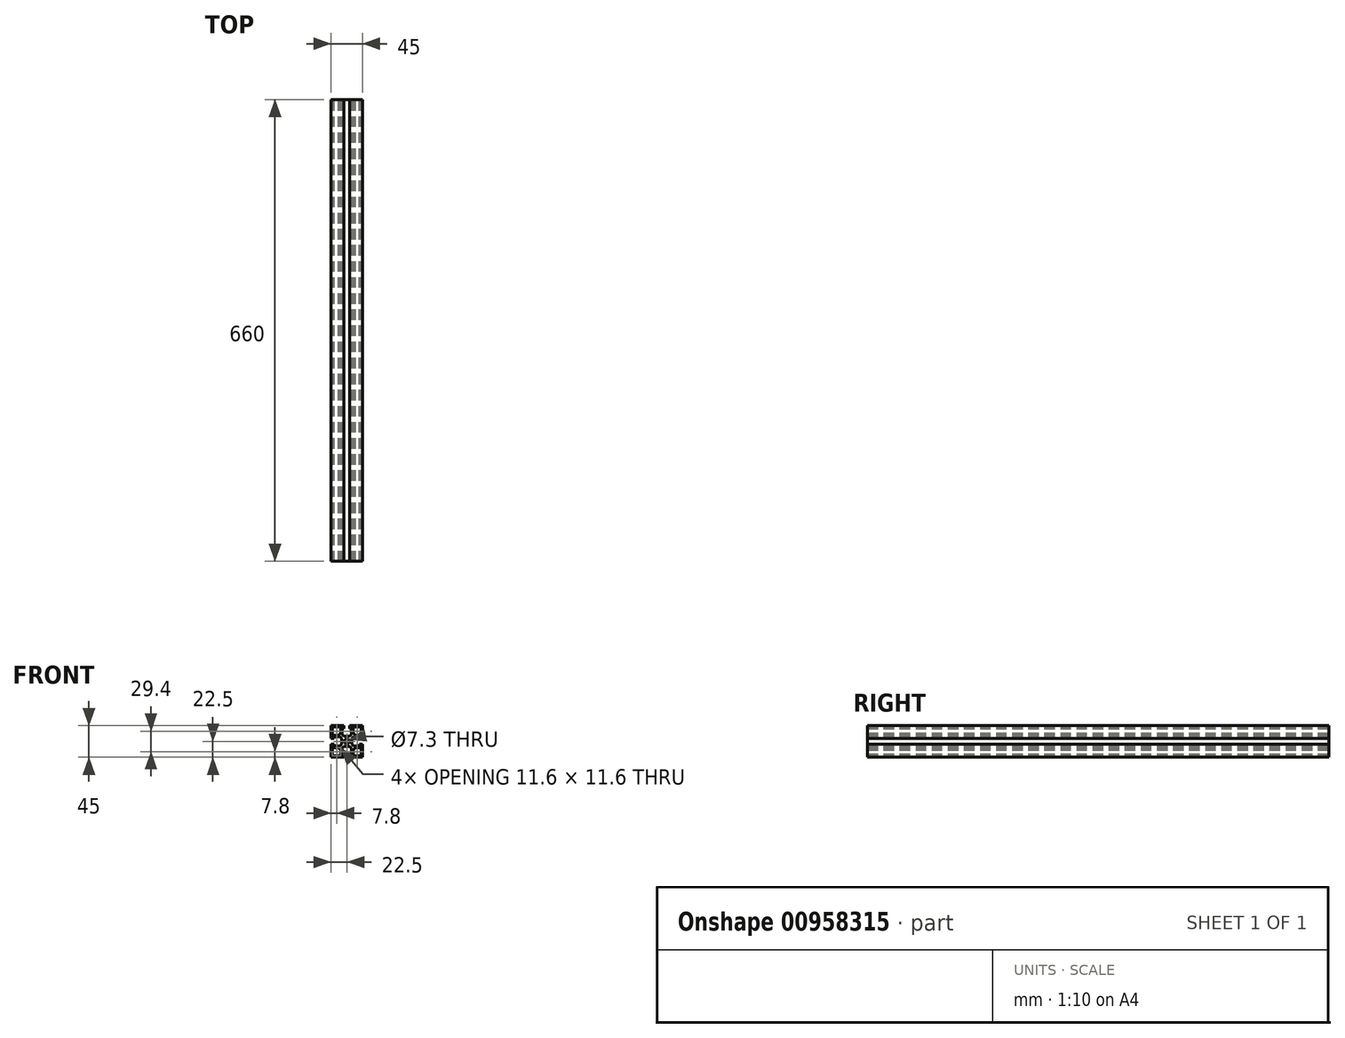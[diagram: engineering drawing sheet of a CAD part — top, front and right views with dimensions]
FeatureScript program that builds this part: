
annotation { "Feature Type Name" : "Feature", "Feature Type Description" : "" }
export const myFeature = defineFeature(function(context is Context, id is Id, definition is map)
    precondition{}
    {
        {
            var Q0;
            Q0=qCreatedBy(makeId("Front.planeOp"),FACE);
            var sketch = newSketch(context, id + "F0", { "sketchPlane" : qUnion([Q0])});
            skLineSegment(sketch, "E0", {"start": v(-22.5, 22.5) * mm, "end": v(-4.15, 22.5) * mm});
            skLineSegment(sketch, "E1", {"start": v(-4.15, 22.5) * mm, "end": v(-4.15, 18) * mm});
            skLineSegment(sketch, "E2", {"start": v(-4.15, 18) * mm, "end": v(-5.75, 18) * mm});
            skArc(sketch, "E3", {"start": v(-5.75, 18) * mm, "mid": v(-6.25, 18.5) * mm, "end": v(-6.75, 18) * mm});
            skLineSegment(sketch, "E4", {"start": v(-6.75, 18) * mm, "end": v(-6.75, 9.8) * mm});
            skLineSegment(sketch, "E5", {"start": v(-6.75, 9.8) * mm, "end": v(-4.15, 7.2) * mm});
            skLineSegment(sketch, "E6", {"start": v(-4.15, 7.2) * mm, "end": v(4.15, 7.2) * mm});
            skLineSegment(sketch, "E7", {"start": v(4.15, 7.2) * mm, "end": v(6.75, 9.8) * mm});
            skLineSegment(sketch, "E8", {"start": v(6.75, 9.8) * mm, "end": v(6.75, 18) * mm});
            skArc(sketch, "E9", {"start": v(6.75, 18) * mm, "mid": v(6.25, 18.5) * mm, "end": v(5.75, 18) * mm});
            skLineSegment(sketch, "E10", {"start": v(5.75, 18) * mm, "end": v(4.15, 18) * mm});
            skLineSegment(sketch, "E11", {"start": v(4.15, 18) * mm, "end": v(4.15, 22.5) * mm});
            skLineSegment(sketch, "E12", {"start": v(4.15, 22.5) * mm, "end": v(22.5, 22.5) * mm});
            skLineSegment(sketch, "E13", {"start": v(22.5, 22.5) * mm, "end": v(22.5, 4.15) * mm});
            skLineSegment(sketch, "E14", {"start": v(22.5, 4.15) * mm, "end": v(18, 4.15) * mm});
            skLineSegment(sketch, "E15", {"start": v(18, 4.15) * mm, "end": v(18, 5.75) * mm});
            skArc(sketch, "E16", {"start": v(18, 5.75) * mm, "mid": v(18.5, 6.25) * mm, "end": v(18, 6.75) * mm});
            skLineSegment(sketch, "E17", {"start": v(18, 6.75) * mm, "end": v(9.8, 6.75) * mm});
            skLineSegment(sketch, "E18", {"start": v(9.8, 6.75) * mm, "end": v(7.2, 4.15) * mm});
            skLineSegment(sketch, "E19", {"start": v(7.2, 4.15) * mm, "end": v(7.2, -4.15) * mm});
            skLineSegment(sketch, "E20", {"start": v(7.2, -4.15) * mm, "end": v(9.8, -6.75) * mm});
            skLineSegment(sketch, "E21", {"start": v(9.8, -6.75) * mm, "end": v(18, -6.75) * mm});
            skArc(sketch, "E22", {"start": v(18, -6.75) * mm, "mid": v(18.5, -6.25) * mm, "end": v(18, -5.75) * mm});
            skLineSegment(sketch, "E23", {"start": v(18, -5.75) * mm, "end": v(18, -4.15) * mm});
            skLineSegment(sketch, "E24", {"start": v(18, -4.15) * mm, "end": v(22.5, -4.15) * mm});
            skLineSegment(sketch, "E25", {"start": v(22.5, -4.15) * mm, "end": v(22.5, -22.5) * mm});
            skLineSegment(sketch, "E26", {"start": v(22.5, -22.5) * mm, "end": v(4.15, -22.5) * mm});
            skLineSegment(sketch, "E27", {"start": v(4.15, -22.5) * mm, "end": v(4.15, -18) * mm});
            skLineSegment(sketch, "E28", {"start": v(4.15, -18) * mm, "end": v(5.75, -18) * mm});
            skArc(sketch, "E29", {"start": v(5.75, -18) * mm, "mid": v(6.25, -18.5) * mm, "end": v(6.75, -18) * mm});
            skLineSegment(sketch, "E30", {"start": v(6.75, -18) * mm, "end": v(6.75, -9.8) * mm});
            skLineSegment(sketch, "E31", {"start": v(6.75, -9.8) * mm, "end": v(4.15, -7.2) * mm});
            skLineSegment(sketch, "E32", {"start": v(4.15, -7.2) * mm, "end": v(-4.15, -7.2) * mm});
            skLineSegment(sketch, "E33", {"start": v(-4.15, -7.2) * mm, "end": v(-6.75, -9.8) * mm});
            skLineSegment(sketch, "E34", {"start": v(-6.75, -9.8) * mm, "end": v(-6.75, -18) * mm});
            skArc(sketch, "E35", {"start": v(-6.75, -18) * mm, "mid": v(-6.25, -18.5) * mm, "end": v(-5.75, -18) * mm});
            skLineSegment(sketch, "E36", {"start": v(-5.75, -18) * mm, "end": v(-4.15, -18) * mm});
            skLineSegment(sketch, "E37", {"start": v(-4.15, -18) * mm, "end": v(-4.15, -22.5) * mm});
            skLineSegment(sketch, "E38", {"start": v(-4.15, -22.5) * mm, "end": v(-22.5, -22.5) * mm});
            skLineSegment(sketch, "E39", {"start": v(-22.5, -22.5) * mm, "end": v(-22.5, -4.15) * mm});
            skLineSegment(sketch, "E40", {"start": v(-22.5, -4.15) * mm, "end": v(-18, -4.15) * mm});
            skLineSegment(sketch, "E41", {"start": v(-18, -4.15) * mm, "end": v(-18, -5.75) * mm});
            skArc(sketch, "E42", {"start": v(-18, -5.75) * mm, "mid": v(-18.5, -6.25) * mm, "end": v(-18, -6.75) * mm});
            skLineSegment(sketch, "E43", {"start": v(-18, -6.75) * mm, "end": v(-9.8, -6.75) * mm});
            skLineSegment(sketch, "E44", {"start": v(-9.8, -6.75) * mm, "end": v(-7.2, -4.15) * mm});
            skLineSegment(sketch, "E45", {"start": v(-7.2, -4.15) * mm, "end": v(-7.2, 4.15) * mm});
            skLineSegment(sketch, "E46", {"start": v(-7.2, 4.15) * mm, "end": v(-9.8, 6.75) * mm});
            skLineSegment(sketch, "E47", {"start": v(-9.8, 6.75) * mm, "end": v(-18, 6.75) * mm});
            skArc(sketch, "E48", {"start": v(-18, 6.75) * mm, "mid": v(-18.5, 6.25) * mm, "end": v(-18, 5.75) * mm});
            skLineSegment(sketch, "E49", {"start": v(-18, 5.75) * mm, "end": v(-18, 4.15) * mm});
            skLineSegment(sketch, "E50", {"start": v(-18, 4.15) * mm, "end": v(-22.5, 4.15) * mm});
            skLineSegment(sketch, "E51", {"start": v(-22.5, 4.15) * mm, "end": v(-22.5, 22.5) * mm});
            skLineSegment(sketch, "E52", {"start": v(-19.5, 20.5) * mm, "end": v(-9.9, 20.5) * mm});
            skArc(sketch, "E53", {"start": v(-8.9, 19.5) * mm, "mid": v(-9.2, 20.2) * mm, "end": v(-9.9, 20.5) * mm});
            skLineSegment(sketch, "E54", {"start": v(-8.9, 19.5) * mm, "end": v(-8.9, 12.1) * mm});
            skLineSegment(sketch, "E55", {"start": v(-8.9, 12.1) * mm, "end": v(-12.1, 8.9) * mm});
            skLineSegment(sketch, "E56", {"start": v(-12.1, 8.9) * mm, "end": v(-19.5, 8.9) * mm});
            skArc(sketch, "E57", {"start": v(-20.5, 9.9) * mm, "mid": v(-20.2, 9.2) * mm, "end": v(-19.5, 8.9) * mm});
            skLineSegment(sketch, "E58", {"start": v(-20.5, 9.9) * mm, "end": v(-20.5, 19.5) * mm});
            skArc(sketch, "E59", {"start": v(-19.5, 20.5) * mm, "mid": v(-20.2, 20.2) * mm, "end": v(-20.5, 19.5) * mm});
            skLineSegment(sketch, "E60", {"start": v(8.9, 12.1) * mm, "end": v(8.9, 19.5) * mm});
            skArc(sketch, "E61", {"start": v(9.9, 20.5) * mm, "mid": v(9.2, 20.2) * mm, "end": v(8.9, 19.5) * mm});
            skLineSegment(sketch, "E62", {"start": v(9.9, 20.5) * mm, "end": v(19.5, 20.5) * mm});
            skArc(sketch, "E63", {"start": v(20.5, 19.5) * mm, "mid": v(20.2, 20.2) * mm, "end": v(19.5, 20.5) * mm});
            skLineSegment(sketch, "E64", {"start": v(20.5, 19.5) * mm, "end": v(20.5, 9.9) * mm});
            skLineSegment(sketch, "E65", {"start": v(19.5, 8.9) * mm, "end": v(12.1, 8.9) * mm});
            skLineSegment(sketch, "E66", {"start": v(12.1, 8.9) * mm, "end": v(8.9, 12.1) * mm});
            skArc(sketch, "E67", {"start": v(19.5, 8.9) * mm, "mid": v(20.2, 9.2) * mm, "end": v(20.5, 9.9) * mm});
            skLineSegment(sketch, "E68", {"start": v(12.1, -8.9) * mm, "end": v(8.9, -12.1) * mm});
            skLineSegment(sketch, "E69", {"start": v(8.9, -12.1) * mm, "end": v(8.9, -19.5) * mm});
            skArc(sketch, "E70", {"start": v(8.9, -19.5) * mm, "mid": v(9.2, -20.2) * mm, "end": v(9.9, -20.5) * mm});
            skLineSegment(sketch, "E71", {"start": v(9.9, -20.5) * mm, "end": v(19.5, -20.5) * mm});
            skLineSegment(sketch, "E72", {"start": v(20.5, -19.5) * mm, "end": v(20.5, -9.9) * mm});
            skArc(sketch, "E73", {"start": v(19.5, -20.5) * mm, "mid": v(20.2, -20.2) * mm, "end": v(20.5, -19.5) * mm});
            skArc(sketch, "E74", {"start": v(20.5, -9.9) * mm, "mid": v(20.2, -9.2) * mm, "end": v(19.5, -8.9) * mm});
            skLineSegment(sketch, "E75", {"start": v(12.1, -8.9) * mm, "end": v(19.5, -8.9) * mm});
            skLineSegment(sketch, "E76", {"start": v(-8.9, -19.5) * mm, "end": v(-8.9, -12.1) * mm});
            skLineSegment(sketch, "E77", {"start": v(-8.9, -12.1) * mm, "end": v(-12.1, -8.9) * mm});
            skLineSegment(sketch, "E78", {"start": v(-12.1, -8.9) * mm, "end": v(-19.5, -8.9) * mm});
            skLineSegment(sketch, "E79", {"start": v(-9.9, -20.5) * mm, "end": v(-19.5, -20.5) * mm});
            skLineSegment(sketch, "E80", {"start": v(-20.5, -19.5) * mm, "end": v(-20.5, -9.9) * mm});
            skArc(sketch, "E81", {"start": v(-19.5, -8.9) * mm, "mid": v(-20.2, -9.2) * mm, "end": v(-20.5, -9.9) * mm});
            skArc(sketch, "E82", {"start": v(-9.9, -20.5) * mm, "mid": v(-9.2, -20.2) * mm, "end": v(-8.9, -19.5) * mm});
            skArc(sketch, "E83", {"start": v(-20.5, -19.5) * mm, "mid": v(-20.2, -20.2) * mm, "end": v(-19.5, -20.5) * mm});
            skCircle(sketch, "E84", {"center": v(0, 0) * mm, "radius": 3.65 * mm});
            skSolve(sketch);
        }
        {
            var Q0;
            Q0=makeQuery(id+"F0.imprint","IMPRINT",FACE,{"disambiguationData":[TD([[makeQuery(id+"F0.imprint","IMPRINT",EDGE,{"derivedFrom":sQuery(id+"F0.wireOp",EDGE,"E0")}),-1.0]])]});
            extrude(context, id + "F1", {"entities" : qUnion([Q0]), "depth" : 660 * mm, "offsetDistance" : 25 * mm});
        }
    });
